# Revit family: 210_Huippuimuri ECo 220P_160__
name_source: partatom
category: Mechanical Equipment
units: mm (PartAtom-declared; Revit-internal decimal feet)

## family parameters
Always vertical = Yes
Cut with Voids When Loaded = No
Part Type = Normal
Room Calculation Point = No
Round Connector Dimension = Use Diameter
Shared = No
Work Plane-Based = No

## types (1)
- VILPE ECo 220P Ø160/700 ROOF FAN
    CAT = 0
    CAT0 = Yes
    D = 160 mm
    D1 = 310 mm  [stored 1.01706 ft]
    D2 = 229 mm
    Default Elevation = 0 mm  [stored 0 ft]
    Description = ECo roof fan
    E1 = 143 mm
    E2 = 145 mm
    H = 700 mm
    H1 = 260 mm
    H11 = 130 mm
    H2 = 344 mm
    H3 = 30 mm  [stored 0.0984252 ft]
    H5 = 52 mm
    H6 = 145 mm
    H7 = 33 mm
    HK = 764 mm
    HP = 174 mm  [stored 0.570866 ft]
    HT = 273 mm
    MC Product Code = VILPE ECo 220P Ø160/700 ROOF FAN
    Manufacturer = Vilpe
    QmdConnectorList = 201;D
    R = 80 mm  [stored 0.262467 ft]
    R1 = 155 mm  [stored 0.50853 ft]
    R2 = 113 mm
    R22 = 108 mm
    R3 = 141 mm
    R4 = 119 mm
    R5 = 141 mm
    R6 = 149 mm
    R7 = 126 mm
    URL = http://www.vilpe.com
    W = 500 mm
    magiPartTypeId = 210
    magiProductFamilyId = Huippuimuri ECo 220P/160/*
    magiProductId = Huippuimuri ECo 220P/160/700

note: [stored X ft] marks values corroborated as IEEE doubles in the binary element streams (Revit-internal decimal feet)

## geometry (parser evidence)
native form markers: Sweep x2
no freeform markers — native parametric forms only
